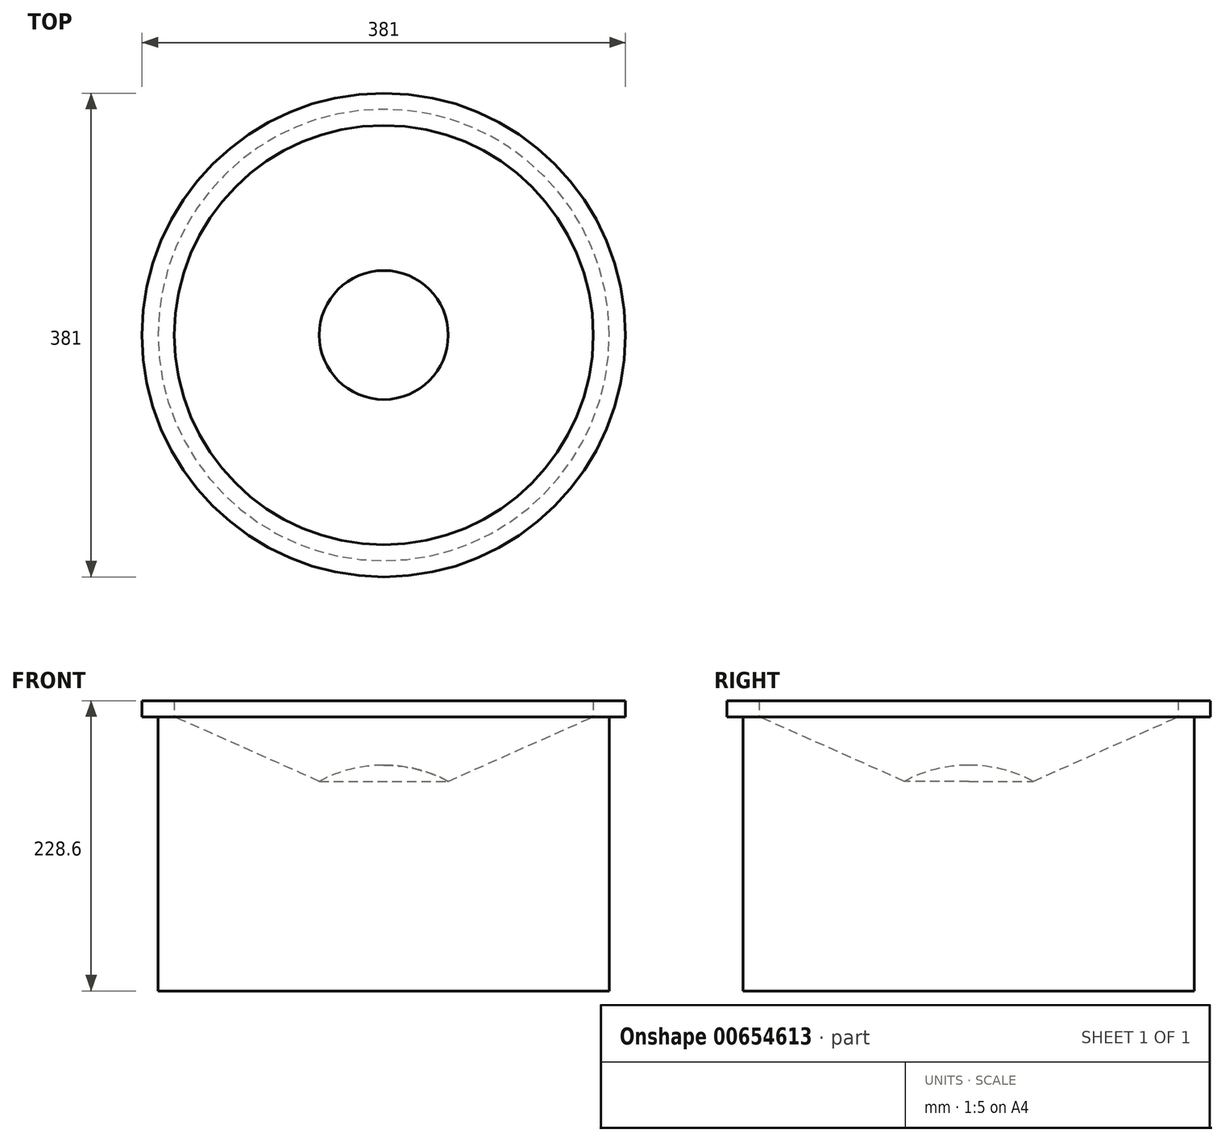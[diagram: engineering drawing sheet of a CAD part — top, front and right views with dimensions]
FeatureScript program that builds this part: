
annotation { "Feature Type Name" : "Feature", "Feature Type Description" : "" }
export const myFeature = defineFeature(function(context is Context, id is Id, definition is map)
    precondition{}
    {
        {
            var Q0;
            Q0=qCreatedBy(makeId("Front.planeOp"),FACE);
            var sketch = newSketch(context, id + "F0", { "sketchPlane" : qUnion([Q0])});
            skLineSegment(sketch, "E0", {"start": v(0, 0) * mm, "end": v(0, 177.8) * mm});
            skLineSegment(sketch, "E1", {"start": v(0, 0) * mm, "end": v(177.8, 0) * mm});
            skLineSegment(sketch, "E2", {"start": v(177.8, 0) * mm, "end": v(177.8, 215.9) * mm});
            skLineSegment(sketch, "E3", {"start": v(177.8, 215.9) * mm, "end": v(190.5, 215.9) * mm});
            skLineSegment(sketch, "E4", {"start": v(190.5, 215.9) * mm, "end": v(190.5, 228.6) * mm});
            skLineSegment(sketch, "E5", {"start": v(190.5, 228.6) * mm, "end": v(165.1, 228.6) * mm});
            skLineSegment(sketch, "E6", {"start": v(165.1, 228.6) * mm, "end": v(165.1, 215.9) * mm});
            skArc(sketch, "E7", {"start": v(50.8, 165.1) * mm, "mid": v(26.18, 174.58) * mm, "end": v(0, 177.8) * mm});
            skLineSegment(sketch, "E8", {"start": v(50.8, 165.1) * mm, "end": v(165.1, 215.9) * mm});
            skSolve(sketch);
        }
        {
            var Q0;
            Q0=makeQuery(id+"F0.imprint","IMPRINT",FACE,{"disambiguationData":[TD([[makeQuery(id+"F0.imprint","IMPRINT",EDGE,{"derivedFrom":sQuery(id+"F0.wireOp",EDGE,"E0")}),-1.0]])]});
            var Q1;
            Q1=sQuery(id+"F0.wireOp",EDGE,"E0");
            revolve(context, id + "F1", {"entities" : qUnion([Q0]), "axis" : qUnion([Q1]), "revolveType" : RevolveType.FULL});
        }
    });
